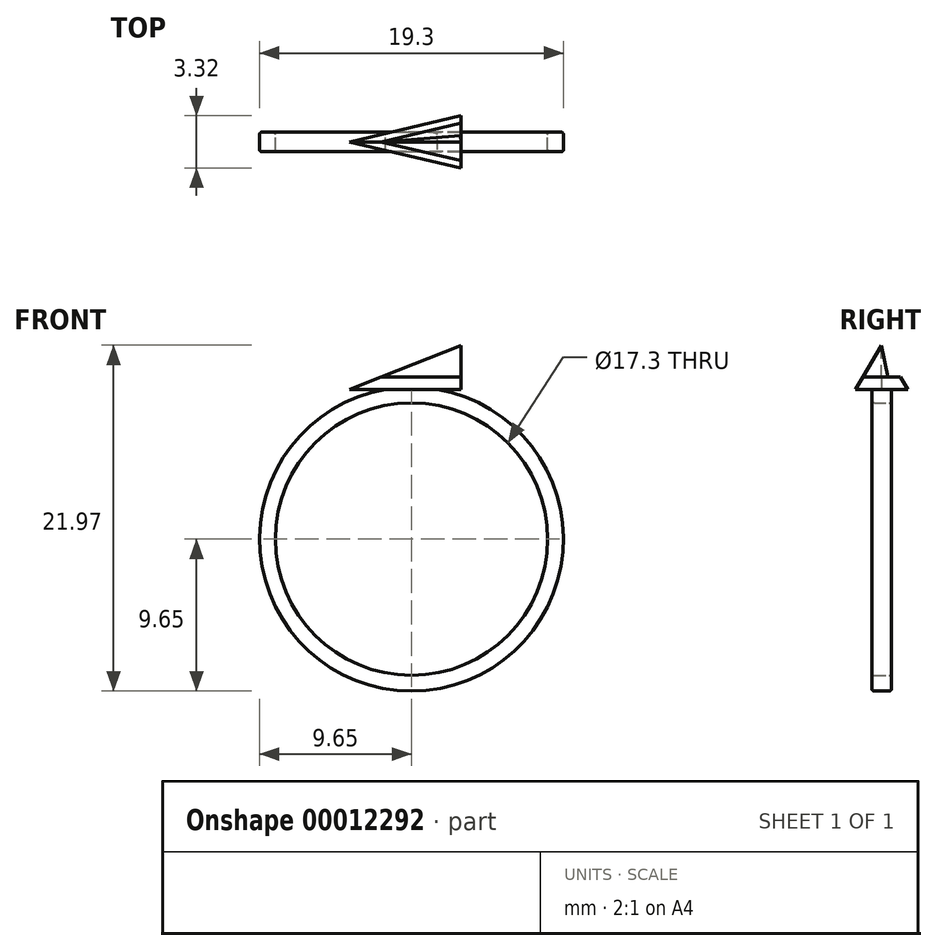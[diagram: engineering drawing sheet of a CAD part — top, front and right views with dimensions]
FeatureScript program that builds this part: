
annotation { "Feature Type Name" : "Feature", "Feature Type Description" : "" }
export const myFeature = defineFeature(function(context is Context, id is Id, definition is map)
    precondition{}
    {
        {
            var Q0;
            Q0=qCreatedBy(makeId("Front.planeOp"),FACE);
            var sketch = newSketch(context, id + "F0", { "sketchPlane" : qUnion([Q0])});
            skCircle(sketch, "E0", {"center": v(0, 0) * mm, "radius": 8.65 * mm});
            skCircle(sketch, "E1", {"center": v(0, 0) * mm, "radius": 9.65 * mm});
            skLineSegment(sketch, "E2", {"start": v(-1.64, 9.5) * mm, "end": v(1.64, 9.5) * mm});
            skLineSegment(sketch, "E3", {"start": v(1.64, 9.5) * mm, "end": v(0, 0) * mm});
            skLineSegment(sketch, "E4", {"start": v(-1.64, 9.5) * mm, "end": v(0, 0) * mm});
            skSolve(sketch);
        }
        {
            var Q0;
            {var subQ1=sQuery(id+"F0.wireOp",EDGE,"E0");var subQ6=sQuery(id+"F0.wireOp",EDGE,"E3");var subQ7=makeQuery(id+"F0.imprint","INTERSECT",VERTEX,{"derivedFrom":[subQ1,subQ6]});Q0=makeQuery(id+"F0.imprint","IMPRINT",FACE,{"disambiguationData":[TD([[makeQuery(id+"F0.imprint","IMPRINT",EDGE,{"disambiguationData":[TD([[subQ7,1.0]])],"derivedFrom":subQ1}),-1.0]])]});}
            var Q1;
            {var subQ4=sQuery(id+"F0.wireOp",EDGE,"E2");Q1=makeQuery(id+"F0.imprint","IMPRINT",FACE,{"disambiguationData":[TD([[makeQuery(id+"F0.imprint","IMPRINT",EDGE,{"derivedFrom":subQ4}),-1.0]])]});}
            extrude(context, id + "F1", {"entities" : qUnion([Q0, Q1]), "depth" : .625 * mm});
        }
        {
            var Q0;
            {var subQ1=sQuery(id+"F0.wireOp",EDGE,"E0");var subQ6=sQuery(id+"F0.wireOp",EDGE,"E3");var subQ7=makeQuery(id+"F0.imprint","INTERSECT",VERTEX,{"derivedFrom":[subQ1,subQ6]});Q0=makeQuery(id+"F0.imprint","IMPRINT",FACE,{"disambiguationData":[TD([[makeQuery(id+"F0.imprint","IMPRINT",EDGE,{"disambiguationData":[TD([[subQ7,1.0]])],"derivedFrom":subQ1}),-1.0]])]});}
            var Q1;
            {var subQ4=sQuery(id+"F0.wireOp",EDGE,"E2");Q1=makeQuery(id+"F0.imprint","IMPRINT",FACE,{"disambiguationData":[TD([[makeQuery(id+"F0.imprint","IMPRINT",EDGE,{"derivedFrom":subQ4}),-1.0]])]});}
            extrude(context, id + "F2", {"entities" : qUnion([Q0, Q1]), "operationType" : NewBodyOperationType.ADD, "oppositeDirection" : true, "depth" : .625 * mm});
        }
        {
            var Q0;
            {var subQ0=sQuery(id+"F0.wireOp",EDGE,"E2");Q0=makeQuery(id+"F2.boolean.opBoolean","MERGE",FACE,{"derivedFrom":[makeQuery(id+"F1.opExtrude","SWEPT_FACE",FACE,{"disambiguationData":[OSD([subQ0])]}),makeQuery(id+"F2.opExtrude","SWEPT_FACE",FACE,{"disambiguationData":[OSD([subQ0])]})]});}
            var sketch = newSketch(context, id + "F3", { "sketchPlane" : qUnion([Q0])});
            skLineSegment(sketch, "E5", {"start": v(3.14, -1.66) * mm, "end": v(-3.94, 0) * mm});
            skLineSegment(sketch, "E6", {"start": v(-3.94, 0) * mm, "end": v(3.14, 1.66) * mm});
            skLineSegment(sketch, "E7", {"start": v(3.14, -1.66) * mm, "end": v(3.14, 1.66) * mm});
            skSolve(sketch);
        }
        {
            var Q0;
            Q0=makeQuery(id+"F2.opExtrude","CAP_EDGE",EDGE,{"disambiguationData":[OSD([sQuery(id+"F0.wireOp",EDGE,"E1")])],"isStart":false});
            var Q1;
            Q1=makeQuery(id+"F2.opExtrude","CAP_EDGE",EDGE,{"disambiguationData":[OSD([sQuery(id+"F0.wireOp",EDGE,"E0")])],"isStart":false});
            var Q2;
            Q2=makeQuery(id+"F1.opExtrude","CAP_EDGE",EDGE,{"disambiguationData":[OSD([sQuery(id+"F0.wireOp",EDGE,"E0")])],"isStart":false});
            var Q3;
            Q3=makeQuery(id+"F1.opExtrude","CAP_EDGE",EDGE,{"disambiguationData":[OSD([sQuery(id+"F0.wireOp",EDGE,"E1")])],"isStart":false});
            fillet(context, id + "F4", {"entities" : qUnion([Q0, Q1, Q2, Q3]), "radius" : .15 * mm, "tangentPropagation" : true, "allowEdgeOverflow" : false});
        }
        {
            var Q0;
            Q0=qSketchRegion(id+"F3",true);
            extrude(context, id + "F5", {"entities" : qUnion([Q0]), "operationType" : NewBodyOperationType.ADD, "depth" : .8 * mm});
        }
        {
            var Q0;
            Q0=makeQuery(id+"F5.opExtrude","CAP_EDGE",EDGE,{"disambiguationData":[OSD([sQuery(id+"F3.wireOp",EDGE,"E5")])],"isStart":false});
            var Q1;
            Q1=makeQuery(id+"F5.opExtrude","CAP_EDGE",EDGE,{"disambiguationData":[OSD([sQuery(id+"F3.wireOp",EDGE,"E6")])],"isStart":false});
            chamfer(context, id + "F6", {"entities" : qUnion([Q0, Q1]), "chamferType" : ChamferType.OFFSET_ANGLE, "width" : .8 * mm, "oppositeDirection" : false, "angle" : 30 * degree, "tangentPropagation" : true});
        }
        {
            var Q0;
            Q0=makeQuery(id+"F6.opChamfer","BLEND_FACE",FACE,{"disambiguationData":[OSD([sQuery(id+"F3.wireOp",EDGE,"E5")])]});
            var sketch = newSketch(context, id + "F7", { "sketchPlane" : qUnion([Q0])});
            skLineSegment(sketch, "E8", {"start": v(4.32, 7.33) * mm, "end": v(4.32, 10.6) * mm});
            skLineSegment(sketch, "E9", {"start": v(-1.19, 8.75) * mm, "end": v(4.32, 10.6) * mm});
            skSolve(sketch);
        }
        {
            var Q0;
            {var subQ0=sQuery(id+"F3.wireOp",EDGE,"E5");var subQ1=makeQuery(id+"F6.opChamfer","BLEND_EDGE",EDGE,{"blendedFrom":[makeQuery(id+"F5.opExtrude","CAP_EDGE",EDGE,{"disambiguationData":[OSD([subQ0])],"isStart":false}),makeQuery(id+"F5.opExtrude","CAP_FACE",FACE,{"disambiguationData":[OSD([subQ0,sQuery(id+"F3.wireOp",EDGE,"E6"),sQuery(id+"F3.wireOp",EDGE,"E7")])],"isStart":false})],"blendedInto":[makeQuery(id+"F5.opExtrude","CAP_FACE",FACE,{"disambiguationData":[OSD([subQ0,sQuery(id+"F3.wireOp",EDGE,"E6"),sQuery(id+"F3.wireOp",EDGE,"E7")])],"isStart":false})]});Q0=makeQuery(id+"F7.imprint","IMPRINT",FACE,{"disambiguationData":[TD([[makeQuery(id+"F7.imprint","IMPRINT",EDGE,{"derivedFrom":subQ1}),1.0]])]});}
            extrude(context, id + "F8", {"entities" : qUnion([Q0]), "oppositeDirection" : true, "depth" : 1.5 * mm});
        }
        {
            var Q0;
            Q0=makeQuery(id+"F8.opExtrude","CAP_EDGE",EDGE,{"disambiguationData":[OSD([sQuery(id+"F3.wireOp",EDGE,"E5"),sQuery(id+"F3.wireOp",EDGE,"E6"),sQuery(id+"F3.wireOp",EDGE,"E7")])],"isStart":false});
            chamfer(context, id + "F9", {"entities" : qUnion([Q0]), "chamferType" : ChamferType.OFFSET_ANGLE, "width" : 1.5 * mm, "oppositeDirection" : false, "angle" : 30 * degree, "tangentPropagation" : true});
        }
        {
            var Q0;
            Q0=makeQuery(id+"F8.opExtrude","CAP_EDGE",EDGE,{"disambiguationData":[OSD([sQuery(id+"F7.wireOp",EDGE,"E8")])],"isStart":false});
            chamfer(context, id + "F10", {"entities" : qUnion([Q0]), "chamferType" : ChamferType.OFFSET_ANGLE, "width" : 1.5 * mm, "oppositeDirection" : false, "angle" : 12.6 * degree, "tangentPropagation" : true});
        }
        {
            var Q0;
            Q0=makeQuery(id+"F8.opExtrude","CAP_EDGE",EDGE,{"disambiguationData":[OSD([sQuery(id+"F7.wireOp",EDGE,"E9")])],"isStart":false});
            chamfer(context, id + "F11", {"entities" : qUnion([Q0]), "chamferType" : ChamferType.OFFSET_ANGLE, "width" : 1.5 * mm, "oppositeDirection" : false, "angle" : 45 * degree, "tangentPropagation" : true});
        }
    });
